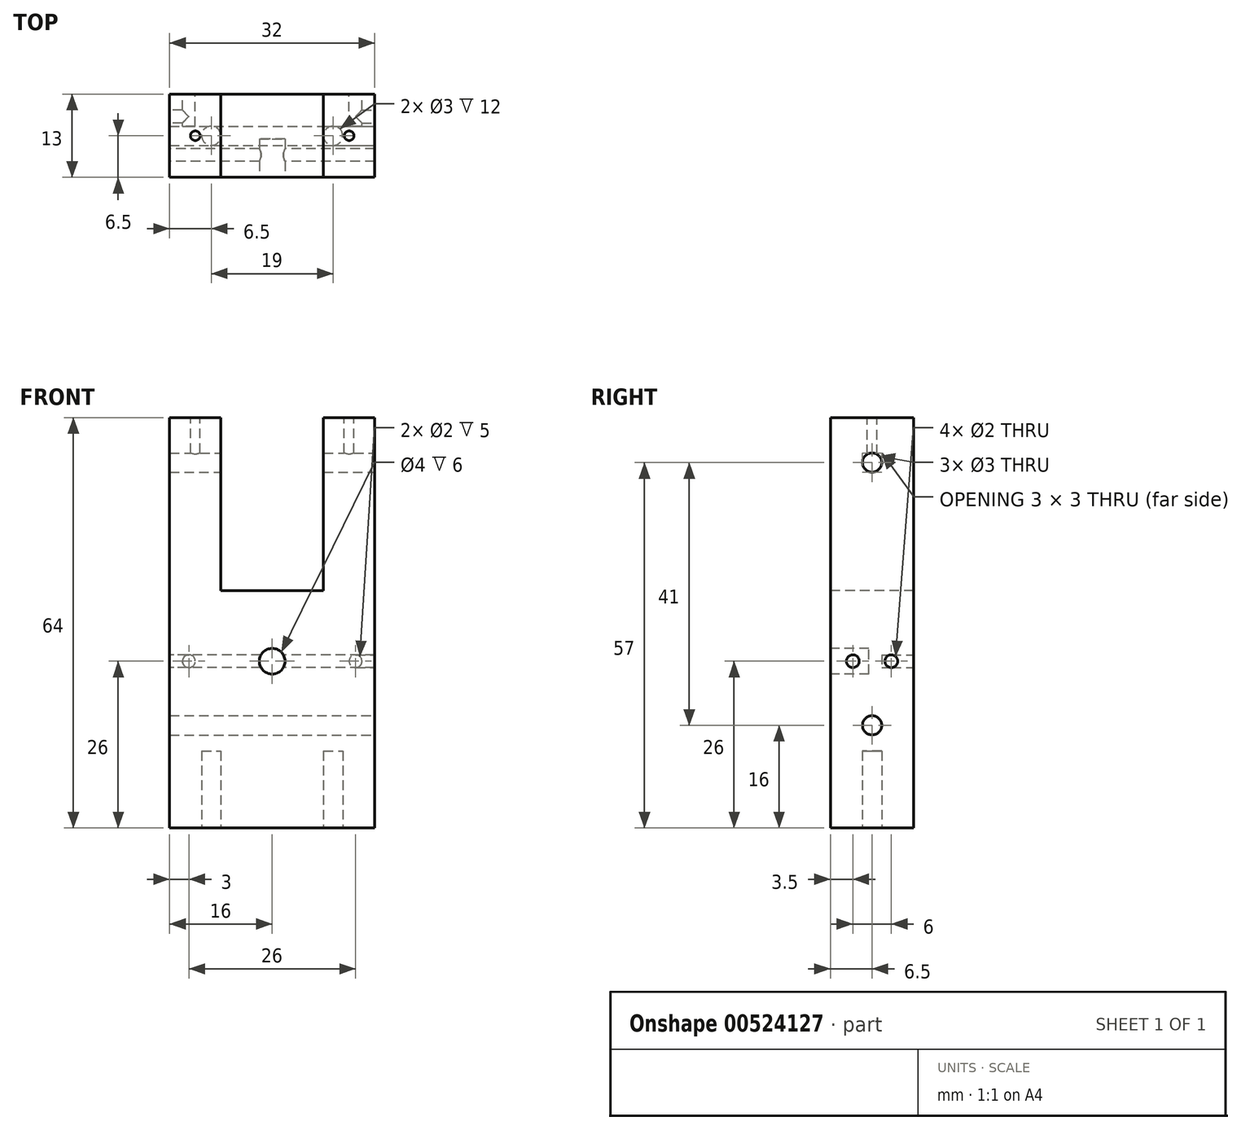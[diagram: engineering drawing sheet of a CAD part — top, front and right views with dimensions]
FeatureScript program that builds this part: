
annotation { "Feature Type Name" : "Feature", "Feature Type Description" : "" }
export const myFeature = defineFeature(function(context is Context, id is Id, definition is map)
    precondition{}
    {
        {
            var Q0;
            Q0=qCreatedBy(makeId("Front.planeOp"),FACE);
            var sketch = newSketch(context, id + "F0", { "sketchPlane" : qUnion([Q0])});
            skLineSegment(sketch, "E0", {"start": v(0, 0) * mm, "end": v(32, 0) * mm});
            skLineSegment(sketch, "E1", {"start": v(32, 0) * mm, "end": v(32, 64) * mm});
            skLineSegment(sketch, "E2", {"start": v(32, 64) * mm, "end": v(24, 64) * mm});
            skLineSegment(sketch, "E3", {"start": v(24, 64) * mm, "end": v(24, 37) * mm});
            skLineSegment(sketch, "E4", {"start": v(24, 37) * mm, "end": v(8, 37) * mm});
            skLineSegment(sketch, "E5", {"start": v(8, 37) * mm, "end": v(8, 64) * mm});
            skLineSegment(sketch, "E6", {"start": v(8, 64) * mm, "end": v(0, 64) * mm});
            skLineSegment(sketch, "E7", {"start": v(0, 64) * mm, "end": v(0, 0) * mm});
            skLineSegment(sketch, "E8", {"start": v(16, 0) * mm, "end": v(16, 68.45) * mm, "construction": true});
            skSolve(sketch);
        }
        {
            var Q0;
            Q0=makeQuery(id+"F0.imprint","IMPRINT",FACE,{"disambiguationData":[TD([[makeQuery(id+"F0.imprint","IMPRINT",EDGE,{"derivedFrom":sQuery(id+"F0.wireOp",EDGE,"E0")}),1.0]])]});
            extrude(context, id + "F1", {"entities" : qUnion([Q0]), "oppositeDirection" : true, "depth" : 13 * mm, "offsetDistance" : 25 * mm});
        }
        {
            var Q0;
            Q0=makeQuery(id+"F1.opExtrude","SWEPT_FACE",FACE,{"disambiguationData":[OSD([sQuery(id+"F0.wireOp",EDGE,"E0")])]});
            var sketch = newSketch(context, id + "F2", { "sketchPlane" : qUnion([Q0])});
            skLineSegment(sketch, "E9", {"start": v(0, -6.5) * mm, "end": v(32, -6.5) * mm, "construction": true});
            skLineSegment(sketch, "E10", {"start": v(16, -13) * mm, "end": v(16, 0) * mm, "construction": true});
            skCircle(sketch, "E11", {"center": v(6.5, -6.5) * mm, "radius": 1.5 * mm});
            skCircle(sketch, "E12", {"center": v(25.5, -6.5) * mm, "radius": 1.5 * mm});
            skSolve(sketch);
        }
        {
            var Q0;
            Q0=makeQuery(id+"F2.imprint","IMPRINT",FACE,{"disambiguationData":[TD([[makeQuery(id+"F2.imprint","IMPRINT",EDGE,{"derivedFrom":sQuery(id+"F2.wireOp",EDGE,"E11")}),1.0]])]});
            var Q1;
            Q1=makeQuery(id+"F2.imprint","IMPRINT",FACE,{"disambiguationData":[TD([[makeQuery(id+"F2.imprint","IMPRINT",EDGE,{"derivedFrom":sQuery(id+"F2.wireOp",EDGE,"E12")}),1.0]])]});
            var Q2;
            Q2=sQuery(id+"F2.wireOp",EDGE,"E11");
            var Q3;
            Q3=sQuery(id+"F2.wireOp",EDGE,"E12");
            extrude(context, id + "F3", {"entities" : qUnion([Q0, Q1]), "operationType" : NewBodyOperationType.REMOVE, "surfaceEntities" : qUnion([Q2, Q3]), "oppositeDirection" : true, "depth" : 12 * mm, "offsetDistance" : 25 * mm});
        }
        {
            var Q0;
            Q0=makeQuery(id+"F1.opExtrude","SWEPT_FACE",FACE,{"disambiguationData":[OSD([sQuery(id+"F0.wireOp",EDGE,"E1")])]});
            var sketch = newSketch(context, id + "F4", { "sketchPlane" : qUnion([Q0])});
            skLineSegment(sketch, "E13", {"start": v(6.5, 0) * mm, "end": v(6.5, 64) * mm, "construction": true});
            skCircle(sketch, "E14", {"center": v(6.5, 57) * mm, "radius": 1.5 * mm});
            skCircle(sketch, "E15", {"center": v(6.5, 16) * mm, "radius": 1.5 * mm});
            skSolve(sketch);
        }
        {
            var Q0;
            Q0=makeQuery(id+"F4.imprint","IMPRINT",FACE,{"disambiguationData":[TD([[makeQuery(id+"F4.imprint","IMPRINT",EDGE,{"derivedFrom":sQuery(id+"F4.wireOp",EDGE,"E14")}),1.0]])]});
            var Q1;
            Q1=sQuery(id+"F4.wireOp",EDGE,"E14");
            extrude(context, id + "F5", {"entities" : qUnion([Q0]), "operationType" : NewBodyOperationType.REMOVE, "surfaceEntities" : qUnion([Q1]), "endBound" : BoundingType.THROUGH_ALL, "oppositeDirection" : true, "depth" : 25 * mm, "offsetDistance" : 25 * mm});
        }
        {
            var Q0;
            Q0=makeQuery(id+"F4.imprint","IMPRINT",FACE,{"disambiguationData":[TD([[makeQuery(id+"F4.imprint","IMPRINT",EDGE,{"derivedFrom":sQuery(id+"F4.wireOp",EDGE,"E15")}),1.0]])]});
            extrude(context, id + "F6", {"entities" : qUnion([Q0]), "operationType" : NewBodyOperationType.REMOVE, "endBound" : BoundingType.THROUGH_ALL, "oppositeDirection" : true, "depth" : 25 * mm, "offsetDistance" : 25 * mm});
        }
        {
            var Q0;
            Q0=makeQuery(id+"F1.opExtrude","CAP_FACE",FACE,{"disambiguationData":[OSD([sQuery(id+"F0.wireOp",EDGE,"E0"),sQuery(id+"F0.wireOp",EDGE,"E1"),sQuery(id+"F0.wireOp",EDGE,"E2"),sQuery(id+"F0.wireOp",EDGE,"E3"),sQuery(id+"F0.wireOp",EDGE,"E4"),sQuery(id+"F0.wireOp",EDGE,"E5"),sQuery(id+"F0.wireOp",EDGE,"E6"),sQuery(id+"F0.wireOp",EDGE,"E7")])],"isStart":true});
            var sketch = newSketch(context, id + "F7", { "sketchPlane" : qUnion([Q0])});
            skLineSegment(sketch, "E16", {"start": v(16, 0) * mm, "end": v(16, 37) * mm, "construction": true});
            skCircle(sketch, "E17", {"center": v(16, 26) * mm, "radius": 2 * mm});
            skSolve(sketch);
        }
        {
            var Q0;
            Q0=makeQuery(id+"F7.imprint","IMPRINT",FACE,{"disambiguationData":[TD([[makeQuery(id+"F7.imprint","IMPRINT",EDGE,{"derivedFrom":sQuery(id+"F7.wireOp",EDGE,"E17")}),1.0]])]});
            var Q1;
            Q1=sQuery(id+"F7.wireOp",EDGE,"E17");
            extrude(context, id + "F8", {"entities" : qUnion([Q0]), "operationType" : NewBodyOperationType.REMOVE, "surfaceEntities" : qUnion([Q1]), "oppositeDirection" : true, "depth" : 6 * mm, "offsetDistance" : 25 * mm});
        }
        {
            var Q0;
            Q0=makeQuery(id+"F1.opExtrude","SWEPT_FACE",FACE,{"disambiguationData":[OSD([sQuery(id+"F0.wireOp",EDGE,"E7")])]});
            var sketch = newSketch(context, id + "F9", { "sketchPlane" : qUnion([Q0])});
            skCircle(sketch, "E18", {"center": v(-3.5, 26) * mm, "radius": 1 * mm});
            skSolve(sketch);
        }
        {
            var Q0;
            Q0=makeQuery(id+"F9.imprint","IMPRINT",FACE,{"disambiguationData":[TD([[makeQuery(id+"F9.imprint","IMPRINT",EDGE,{"derivedFrom":sQuery(id+"F9.wireOp",EDGE,"E18")}),1.0]])]});
            extrude(context, id + "F10", {"entities" : qUnion([Q0]), "operationType" : NewBodyOperationType.REMOVE, "endBound" : BoundingType.THROUGH_ALL, "oppositeDirection" : true, "depth" : 25 * mm, "offsetDistance" : 25 * mm});
        }
        {
            var Q0;
            Q0=makeQuery(id+"F1.opExtrude","CAP_FACE",FACE,{"disambiguationData":[OSD([sQuery(id+"F0.wireOp",EDGE,"E0"),sQuery(id+"F0.wireOp",EDGE,"E1"),sQuery(id+"F0.wireOp",EDGE,"E2"),sQuery(id+"F0.wireOp",EDGE,"E3"),sQuery(id+"F0.wireOp",EDGE,"E4"),sQuery(id+"F0.wireOp",EDGE,"E5"),sQuery(id+"F0.wireOp",EDGE,"E6"),sQuery(id+"F0.wireOp",EDGE,"E7")])],"isStart":false});
            var sketch = newSketch(context, id + "F11", { "sketchPlane" : qUnion([Q0])});
            skCircle(sketch, "E19", {"center": v(-29, 26) * mm, "radius": 1 * mm});
            skCircle(sketch, "E20", {"center": v(-3, 26) * mm, "radius": 1 * mm});
            skSolve(sketch);
        }
        {
            var Q0;
            Q0=makeQuery(id+"F11.imprint","IMPRINT",FACE,{"disambiguationData":[TD([[makeQuery(id+"F11.imprint","IMPRINT",EDGE,{"derivedFrom":sQuery(id+"F11.wireOp",EDGE,"E19")}),1.0]])]});
            var Q1;
            Q1=makeQuery(id+"F11.imprint","IMPRINT",FACE,{"disambiguationData":[TD([[makeQuery(id+"F11.imprint","IMPRINT",EDGE,{"derivedFrom":sQuery(id+"F11.wireOp",EDGE,"E20")}),1.0]])]});
            extrude(context, id + "F12", {"entities" : qUnion([Q0, Q1]), "operationType" : NewBodyOperationType.REMOVE, "oppositeDirection" : true, "depth" : 5 * mm, "offsetDistance" : 25 * mm});
        }
        {
            var Q0;
            Q0=makeQuery(id+"F1.opExtrude","SWEPT_FACE",FACE,{"disambiguationData":[OSD([sQuery(id+"F0.wireOp",EDGE,"E7")])]});
            var sketch = newSketch(context, id + "F13", { "sketchPlane" : qUnion([Q0])});
            skCircle(sketch, "E21", {"center": v(-9.5, 26) * mm, "radius": 1 * mm});
            skSolve(sketch);
        }
        {
            var Q0;
            Q0=makeQuery(id+"F13.imprint","IMPRINT",FACE,{"disambiguationData":[TD([[makeQuery(id+"F13.imprint","IMPRINT",EDGE,{"derivedFrom":sQuery(id+"F13.wireOp",EDGE,"E21")}),1.0]])]});
            extrude(context, id + "F14", {"entities" : qUnion([Q0]), "operationType" : NewBodyOperationType.REMOVE, "endBound" : BoundingType.UP_TO_NEXT, "oppositeDirection" : true, "depth" : 25 * mm, "offsetDistance" : 25 * mm});
        }
        {
            var Q0;
            Q0=makeQuery(id+"F4.imprint","IMPRINT",FACE,{"disambiguationData":[TD([[makeQuery(id+"F4.imprint","IMPRINT",EDGE,{"derivedFrom":sQuery(id+"F4.wireOp",EDGE,"E14")}),-1.0]])]});
            var sketch = newSketch(context, id + "F15", { "sketchPlane" : qUnion([Q0])});
            skCircle(sketch, "E22", {"center": v(9.5, 26) * mm, "radius": 1 * mm});
            skSolve(sketch);
        }
        {
            var Q0;
            Q0=makeQuery(id+"F15.imprint","IMPRINT",FACE,{"disambiguationData":[TD([[makeQuery(id+"F15.imprint","IMPRINT",EDGE,{"derivedFrom":sQuery(id+"F15.wireOp",EDGE,"E22")}),1.0]])]});
            extrude(context, id + "F16", {"entities" : qUnion([Q0]), "operationType" : NewBodyOperationType.REMOVE, "endBound" : BoundingType.UP_TO_NEXT, "oppositeDirection" : true, "depth" : 25 * mm, "offsetDistance" : 25 * mm});
        }
        {
            var Q0;
            Q0=makeQuery(id+"F1.opExtrude","SWEPT_FACE",FACE,{"disambiguationData":[OSD([sQuery(id+"F0.wireOp",EDGE,"E6")])]});
            var sketch = newSketch(context, id + "F17", { "sketchPlane" : qUnion([Q0])});
            skLineSegment(sketch, "E23", {"start": v(0, 6.5) * mm, "end": v(32.42, 6.5) * mm, "construction": true});
            skPoint(sketch, "E23.endSnap0", {"position": v(0, 6.5) * mm});
            skCircle(sketch, "E24", {"center": v(4, 6.5) * mm, "radius": 0.75 * mm});
            skCircle(sketch, "E25", {"center": v(28, 6.5) * mm, "radius": 0.75 * mm});
            skLineSegment(sketch, "E26", {"start": v(28, 13.83) * mm, "end": v(28, 0) * mm, "construction": true});
            skSolve(sketch);
        }
        {
            var Q0;
            Q0=makeQuery(id+"F17.imprint","IMPRINT",FACE,{"disambiguationData":[TD([[makeQuery(id+"F17.imprint","IMPRINT",EDGE,{"derivedFrom":sQuery(id+"F17.wireOp",EDGE,"E24")}),1.0]])]});
            var Q1;
            Q1=makeQuery(id+"F17.imprint","IMPRINT",FACE,{"disambiguationData":[TD([[makeQuery(id+"F17.imprint","IMPRINT",EDGE,{"derivedFrom":sQuery(id+"F17.wireOp",EDGE,"E25")}),1.0]])]});
            extrude(context, id + "F18", {"entities" : qUnion([Q0, Q1]), "operationType" : NewBodyOperationType.REMOVE, "endBound" : BoundingType.UP_TO_NEXT, "oppositeDirection" : true, "depth" : 25 * mm, "offsetDistance" : 25 * mm});
        }
    });
